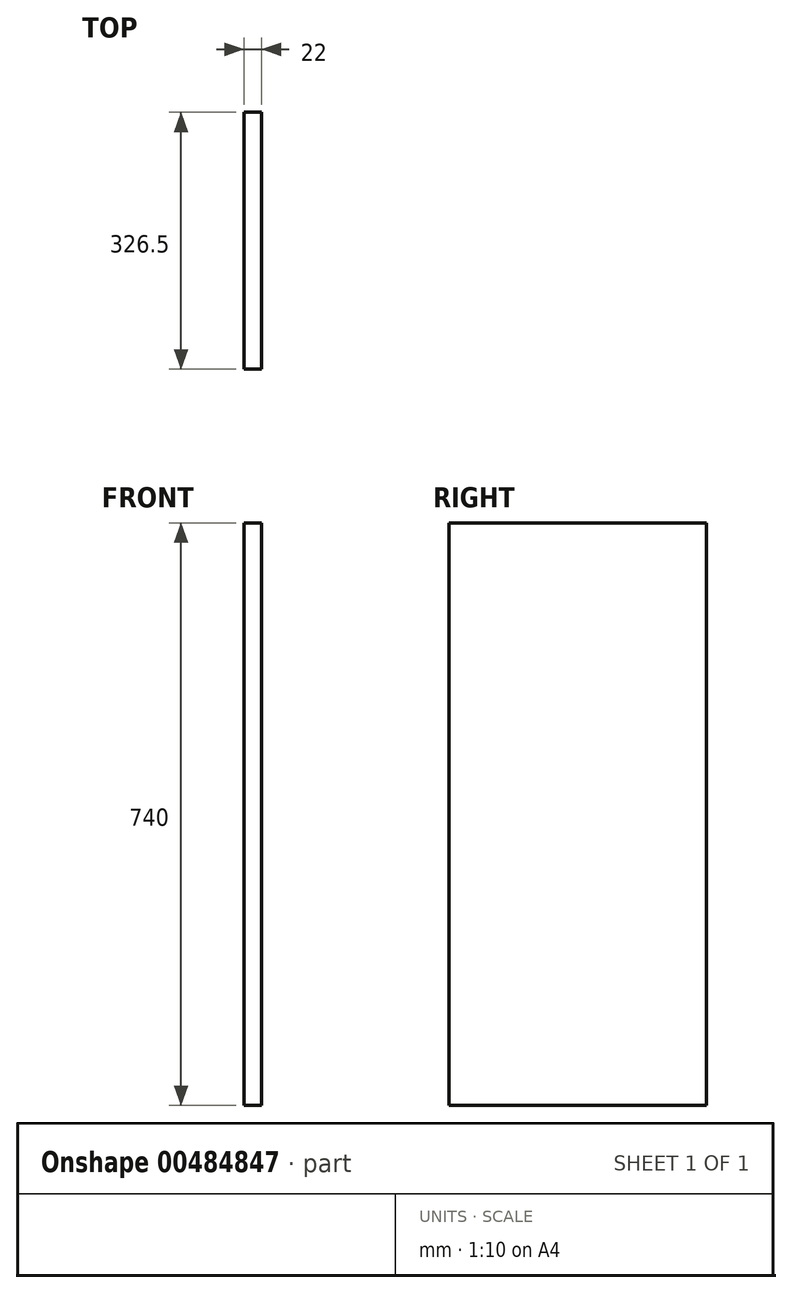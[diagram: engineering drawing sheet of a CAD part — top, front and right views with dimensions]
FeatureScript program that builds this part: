
annotation { "Feature Type Name" : "Feature", "Feature Type Description" : "" }
export const myFeature = defineFeature(function(context is Context, id is Id, definition is map)
    precondition{}
    {
        {
            var Q0;
            Q0=qCreatedBy(makeId("Right.planeOp"),FACE);
            var sketch = newSketch(context, id + "F0", { "sketchPlane" : qUnion([Q0])});
            skLineSegment(sketch, "E0.bottom", {"start": v(-303.88, 408.02) * mm, "end": v(22.62, 408.02) * mm});
            skLineSegment(sketch, "E0.top", {"start": v(-303.88, -331.98) * mm, "end": v(22.62, -331.98) * mm});
            skLineSegment(sketch, "E0.left", {"start": v(-303.88, 408.02) * mm, "end": v(-303.88, -331.98) * mm});
            skLineSegment(sketch, "E0.right", {"start": v(22.62, 408.02) * mm, "end": v(22.62, -331.98) * mm});
            skSolve(sketch);
        }
        {
            var Q0;
            Q0 = qSketchRegion(id + "F0", true);
            extrude(context, id + "F1", {"entities" : qUnion([Q0]), "depth" : 22 * mm});
        }
    });
